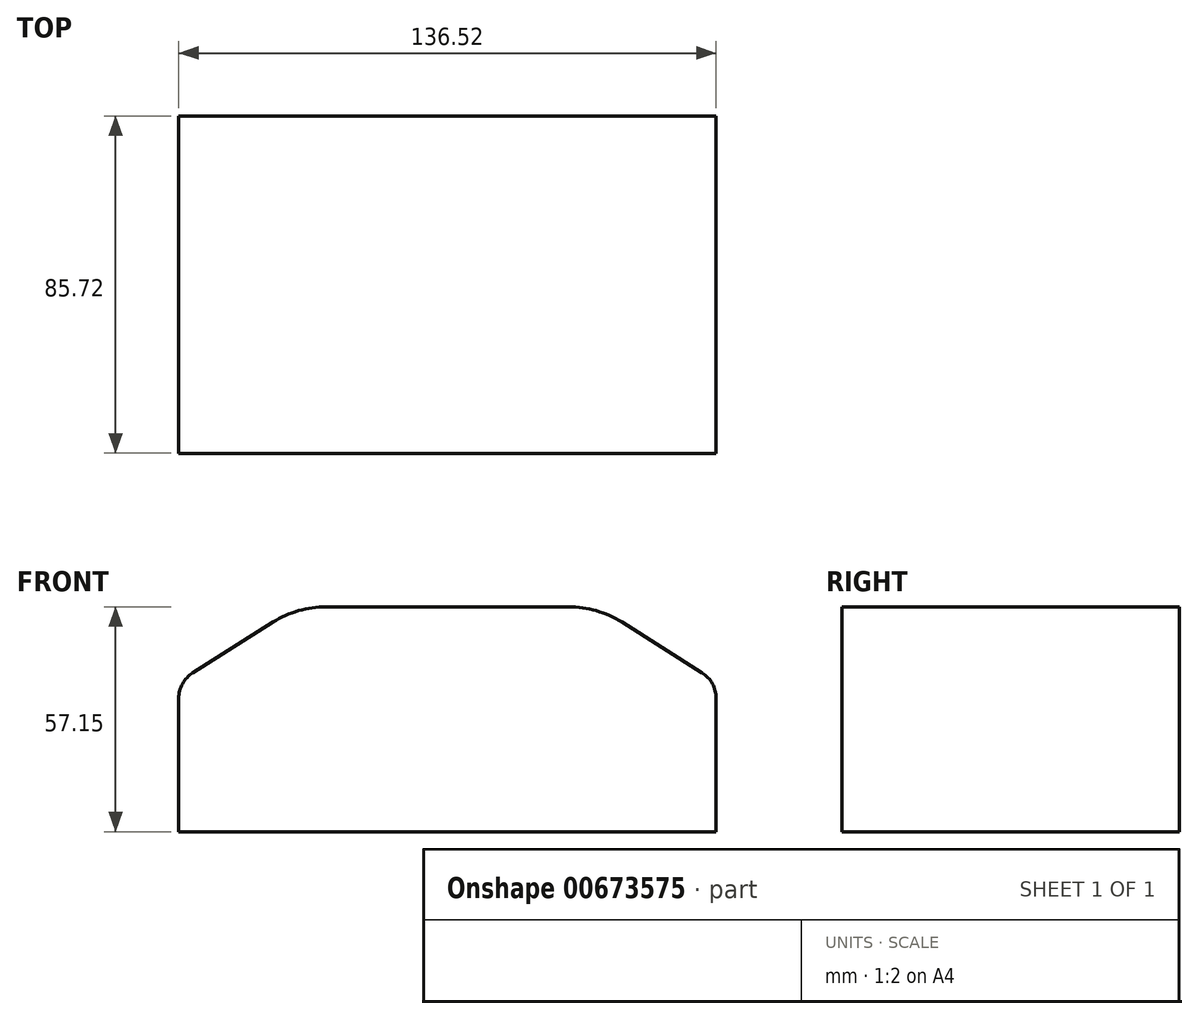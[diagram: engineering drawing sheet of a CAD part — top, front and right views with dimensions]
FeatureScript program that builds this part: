
annotation { "Feature Type Name" : "Feature", "Feature Type Description" : "" }
export const myFeature = defineFeature(function(context is Context, id is Id, definition is map)
    precondition{}
    {
        {
            var Q0;
            Q0=qCreatedBy(makeId("Front.planeOp"),FACE);
            var sketch = newSketch(context, id + "F0", { "sketchPlane" : qUnion([Q0])});
            skLineSegment(sketch, "E0", {"start": v(0, 0) * mm, "end": v(68.26, 0) * mm});
            skLineSegment(sketch, "E1", {"start": v(68.26, 0) * mm, "end": v(68.26, 38.1) * mm});
            skLineSegment(sketch, "E2", {"start": v(68.26, 38.1) * mm, "end": v(38.1, 57.15) * mm});
            skLineSegment(sketch, "E3", {"start": v(38.1, 57.15) * mm, "end": v(0, 57.15) * mm});
            skLineSegment(sketch, "E4.MirrorCS", {"start": v(0, 0) * mm, "end": v(-68.26, 0) * mm});
            skLineSegment(sketch, "E5.MirrorCS", {"start": v(-68.26, 0) * mm, "end": v(-68.26, 38.1) * mm});
            skLineSegment(sketch, "E6.MirrorCS", {"start": v(-38.1, 57.15) * mm, "end": v(0, 57.15) * mm});
            skLineSegment(sketch, "E7.MirrorCS", {"start": v(-68.26, 38.1) * mm, "end": v(-38.1, 57.15) * mm});
            skSolve(sketch);
        }
        {
            var Q0;
            Q0=makeQuery(id+"F0.imprint","IMPRINT",FACE,{"disambiguationData":[TD([[makeQuery(id+"F0.imprint","IMPRINT",EDGE,{"derivedFrom":sQuery(id+"F0.wireOp",EDGE,"E0")}),1.0]])]});
            extrude(context, id + "F1", {"entities" : qUnion([Q0]), "depth" : 85.72 * mm, "offsetDistance" : 25.4 * mm});
        }
        {
            var Q0;
            Q0=makeQuery(id+"F1.opExtrude","SWEPT_EDGE",EDGE,{"disambiguationData":[OSD([sQuery(id+"F0.wireOp",EDGE,"E5.MirrorCS"),sQuery(id+"F0.wireOp",EDGE,"E7.MirrorCS")])]});
            fillet(context, id + "F2", {"entities" : qUnion([Q0]), "radius" : 7.62 * mm, "tangentPropagation" : true, "allowEdgeOverflow" : false});
        }
        {
            var Q0;
            Q0=makeQuery(id+"F1.opExtrude","SWEPT_EDGE",EDGE,{"disambiguationData":[OSD([sQuery(id+"F0.wireOp",EDGE,"E6.MirrorCS"),sQuery(id+"F0.wireOp",EDGE,"E7.MirrorCS")])]});
            fillet(context, id + "F3", {"entities" : qUnion([Q0]), "radius" : 25.4 * mm, "tangentPropagation" : true, "allowEdgeOverflow" : false});
        }
        {
            var Q0;
            Q0=makeQuery(id+"F1.opExtrude","SWEPT_EDGE",EDGE,{"disambiguationData":[OSD([sQuery(id+"F0.wireOp",EDGE,"E2"),sQuery(id+"F0.wireOp",EDGE,"E3")])]});
            fillet(context, id + "F4", {"entities" : qUnion([Q0]), "radius" : 25.4 * mm, "tangentPropagation" : true, "allowEdgeOverflow" : false});
        }
        {
            var Q0;
            Q0=makeQuery(id+"F1.opExtrude","SWEPT_EDGE",EDGE,{"disambiguationData":[OSD([sQuery(id+"F0.wireOp",EDGE,"E1"),sQuery(id+"F0.wireOp",EDGE,"E2")])]});
            fillet(context, id + "F5", {"entities" : qUnion([Q0]), "radius" : 7.62 * mm, "tangentPropagation" : true, "allowEdgeOverflow" : false});
        }
    });
